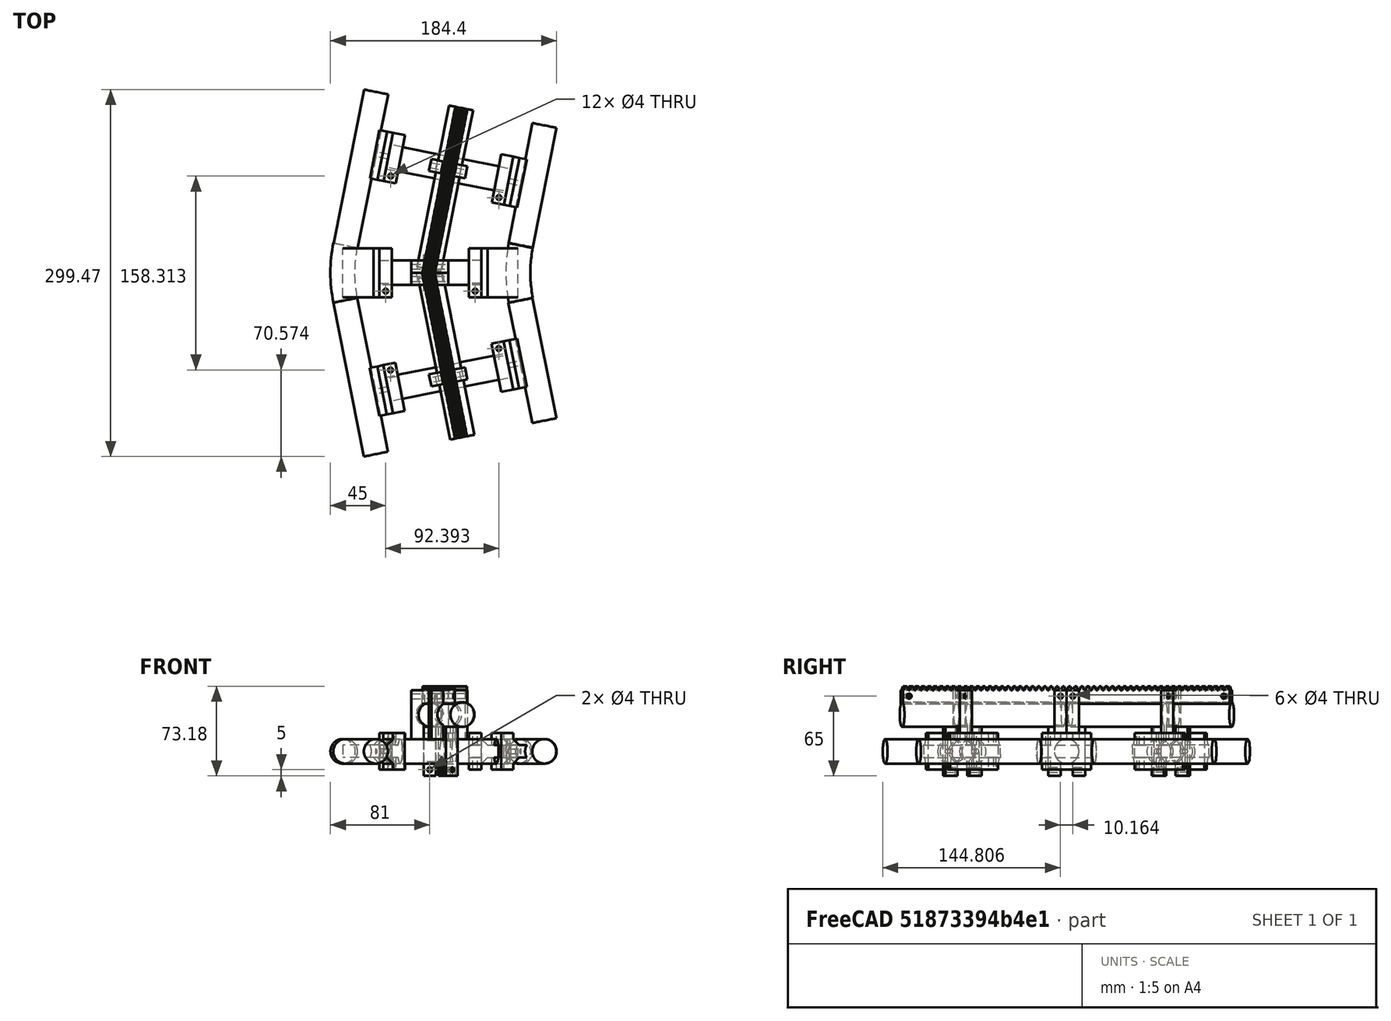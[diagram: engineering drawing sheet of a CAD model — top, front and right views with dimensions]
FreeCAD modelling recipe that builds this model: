
FCSTD DOCUMENT  (FreeCAD 0.17R13522 (Git))
Label: turn
License: All rights reserved
LicenseURL: http://en.wikipedia.org/wiki/All_rights_reserved
objects: Part::FeaturePython×15, Part::Cylinder×9, Part::Compound×3
note: 27 computed .brp shape members not serialized (recipe doc carries the construction recipe); baked Part::Feature solids carry a one-line shape summary decoded from their .brp

FEATURE [Part::FeaturePython] turninner_01  # a2plus imported part (geometry in sourceFile) (typed FeaturePython)
  Placement = pos=(57,0,0) rot=(0,0,1;0rad)
  fixedPosition = true
  sourceFile = <userpath>/repo/mavis/parts/turninner.fcstd
  timeLastImport = 1.53898e+09
  updateColors = true
FEATURE [Part::FeaturePython] turnouter_01  # a2plus imported part (geometry in sourceFile) (typed FeaturePython)
  Placement = pos=(-86,0,0) rot=(0,0,1;0rad)
  fixedPosition = false
  sourceFile = <userpath>/repo/mavis/parts/turnouter.fcstd
  timeLastImport = 1.53898e+09
  updateColors = true
FEATURE [Part::FeaturePython] sleeperinner_01  # a2plus imported part (geometry in sourceFile) (typed FeaturePython)
  Placement = pos=(-45,0,0) rot=(0.57735,-0.57735,-0.57735;2.0944rad)
  fixedPosition = false
  sourceFile = <userpath>/repo/mavis/parts/sleeperinner.fcstd
  timeLastImport = 1.53614e+09
  updateColors = true
FEATURE [Part::Cylinder] Cylinder
  Angle = 360
  AttacherType = Attacher::AttachEngine3D
  Height = 100
  Placement = pos=(-50,0,0) rot=(0.57735,-0.57735,0.57735;4.18879rad)
  Radius = 10
FEATURE [Part::Cylinder] Cylinder001  label="Outer Rail"
  Angle = 360
  AttacherType = Attacher::AttachEngine3D
  Height = 128
  Placement = pos=(-70,-50,0) rot=(-1,0,0;1.5708rad)
  Radius = 10
FEATURE [Part::FeaturePython] sleeperinner_002  # a2plus imported part (geometry in sourceFile) (typed FeaturePython)
  Placement = pos=(45,0,0) rot=(0.57735,-0.57735,0.57735;4.18879rad)
  fixedPosition = false
  sourceFile = <userpath>/repo/mavis/parts/sleeperinner.fcstd
  timeLastImport = 1.53614e+09
  updateColors = true
FEATURE [Part::Cylinder] Cylinder002
  Angle = 360
  AttacherType = Attacher::AttachEngine3D
  Height = 100
  Placement = pos=(70,-50,0) rot=(-1,0,0;1.5708rad)
  Radius = 10
FEATURE [Part::Cylinder] Cylinder003
  Angle = 360
  AttacherType = Attacher::AttachEngine3D
  Height = 83
  Placement = pos=(27,0,0) rot=(0,-1,0;1.5708rad)
  Radius = 10
FEATURE [Part::FeaturePython] fastener_middleturn_20mm_01  # a2plus imported part (geometry in sourceFile) (typed FeaturePython)
  Placement = pos=(-15,-5,30) rot=(0.57735,0.57735,-0.57735;2.0944rad)
  fixedPosition = false
  sourceFile = <userpath>/repo/mavis/parts/fastener-middleturn-20mm.fcstd
  timeLastImport = 1.53898e+09
  updateColors = true
FEATURE [Part::FeaturePython] fastener_join_20mm_01  # a2plus imported part (geometry in sourceFile) (typed FeaturePython)
  Placement = pos=(-15,0,0) rot=(0,-1,0;1.5708rad)
  fixedPosition = false
  sourceFile = <userpath>/repo/mavis/parts/fastener-join-20mm.fcstd
  timeLastImport = 1.53614e+09
  updateColors = true
FEATURE [Part::FeaturePython] fastener_middleturn_rev_20mm_01  # a2plus imported part (geometry in sourceFile) (typed FeaturePython)
  Placement = pos=(-15,5,30) rot=(0.57735,0.57735,-0.57735;2.0944rad)
  fixedPosition = false
  sourceFile = <userpath>/repo/mavis/parts/fastener-middleturn-rev-20mm.fcstd
  timeLastImport = 1.53898e+09
  updateColors = true
FEATURE [Part::FeaturePython] fastener_join_20mm_01001  # a2plus imported part (geometry in sourceFile) (typed FeaturePython)
  Placement = pos=(0,-85,0) rot=(0.09755,-0.990438,0.09755;1.5804rad)
  fixedPosition = false
  sourceFile = <userpath>/repo/mavis/parts/fastener-join-20mm.fcstd
  timeLastImport = 1.53614e+09
  updateColors = true
FEATURE [Part::FeaturePython] fastener_join_20mm_01002  # a2plus imported part (geometry in sourceFile) (typed FeaturePython)
  Placement = pos=(0,85,30) rot=(-0.611588,-0.501917,0.611588;4.07195rad)
  fixedPosition = false
  sourceFile = <userpath>/repo/mavis/parts/fastener-join-20mm.fcstd
  timeLastImport = 1.53614e+09
  updateColors = true
FEATURE [Part::FeaturePython] fastener_join_20mm_01003  # a2plus imported part (geometry in sourceFile) (typed FeaturePython)
  Placement = pos=(0,85,0) rot=(0.705398,-0.069476,0.705398;3.00286rad)
  fixedPosition = false
  sourceFile = <userpath>/repo/mavis/parts/fastener-join-20mm.fcstd
  timeLastImport = 1.53614e+09
  updateColors = true
FEATURE [Part::FeaturePython] fastener_join_20mm_01004  # a2plus imported part (geometry in sourceFile) (typed FeaturePython)
  Placement = pos=(0,-85,30) rot=(0.611588,-0.501917,-0.611588;4.07195rad)
  fixedPosition = false
  sourceFile = <userpath>/repo/mavis/parts/fastener-join-20mm.fcstd
  timeLastImport = 1.53614e+09
  updateColors = true
FEATURE [Part::Cylinder] Cylinder004
  Angle = 360
  AttacherType = Attacher::AttachEngine3D
  Height = 134
  Placement = pos=(-15.6926,3.12145,30) rot=(-0.990438,0.09755,-0.09755;1.5804rad)
  Radius = 10
FEATURE [Part::Cylinder] Cylinder005
  Angle = 360
  AttacherType = Attacher::AttachEngine3D
  Height = 134
  Placement = pos=(-14.522,-2.76327,30) rot=(-0.069476,0.705398,-0.705398;3.00286rad)
  Radius = 10
FEATURE [Part::FeaturePython] turnrack_01  # a2plus imported part (geometry in sourceFile) (typed FeaturePython)
  Placement = pos=(15.3759,-133.353,40) rot=(0.09755,-0.990438,0.09755;1.5804rad)
  fixedPosition = false
  sourceFile = <userpath>/repo/mavis/parts/turnrack.fcstd
  timeLastImport = 1.53898e+09
  updateColors = true
FEATURE [Part::FeaturePython] turnrack_rev_01  # a2plus imported part (geometry in sourceFile) (typed FeaturePython)
  Placement = pos=(15.5953,132.968,40) rot=(0.705398,-0.069476,0.705398;3.00286rad)
  fixedPosition = false
  sourceFile = <userpath>/repo/mavis/parts/turnrack-rev.fcstd
  timeLastImport = 1.53898e+09
  updateColors = true
FEATURE [Part::Compound] Compound  label="Piece Compound"
  Links = -> [Cylinder001,sleeperinner_01,Cylinder,sleeperinner_002,Cylinder002]
  Placement = pos=(0,-85.3283,0) rot=(0,0,1;0.19635rad)
FEATURE [Part::Cylinder] Cylinder006
  Angle = 360
  AttacherType = Attacher::AttachEngine3D
  Height = 100
  Placement = pos=(70,-50,0) rot=(-1,0,0;1.5708rad)
  Radius = 10
FEATURE [Part::FeaturePython] sleeperinner_003  # a2plus imported part (geometry in sourceFile) (typed FeaturePython)
  Placement = pos=(45,0,0) rot=(0.57735,-0.57735,0.57735;4.18879rad)
  fixedPosition = false
  sourceFile = <userpath>/repo/mavis/parts/sleeperinner.fcstd
  timeLastImport = 1.53614e+09
  updateColors = true
FEATURE [Part::Cylinder] Cylinder007
  Angle = 360
  AttacherType = Attacher::AttachEngine3D
  Height = 100
  Placement = pos=(-50,0,0) rot=(0.57735,-0.57735,0.57735;4.18879rad)
  Radius = 10
FEATURE [Part::FeaturePython] sleeperinner_004  # a2plus imported part (geometry in sourceFile) (typed FeaturePython)
  Placement = pos=(-45,0,0) rot=(0.57735,-0.57735,-0.57735;2.0944rad)
  fixedPosition = false
  sourceFile = <userpath>/repo/mavis/parts/sleeperinner.fcstd
  timeLastImport = 1.53614e+09
  updateColors = true
FEATURE [Part::Cylinder] Cylinder008  label="Outer Rail001"
  Angle = 360
  AttacherType = Attacher::AttachEngine3D
  Height = 128
  Placement = pos=(-70,-50,0) rot=(-1,0,0;1.5708rad)
  Radius = 10
FEATURE [Part::Compound] Compound001  label="Piece Compound001"
  Links = -> [Cylinder008,sleeperinner_004,Cylinder007,sleeperinner_003,Cylinder006]
  Placement = pos=(0.184423,84.8505,0) rot=(0.995185,-0.098017,0;3.14159rad)
FEATURE [Part::Compound] Compound002
  Links = -> [turninner_01,fastener_join_20mm_01003,turnouter_01,fastener_middleturn_rev_20mm_01,turnrack_rev_01,Cylinder003,Compound001,fastener_middleturn_20mm_01,Cylinder004,fastener_join_20mm_01001,fastener_join_20mm_01,Cylinder005,Compound,turnrack_01,fastener_join_20mm_01004,fastener_join_20mm_01002]
